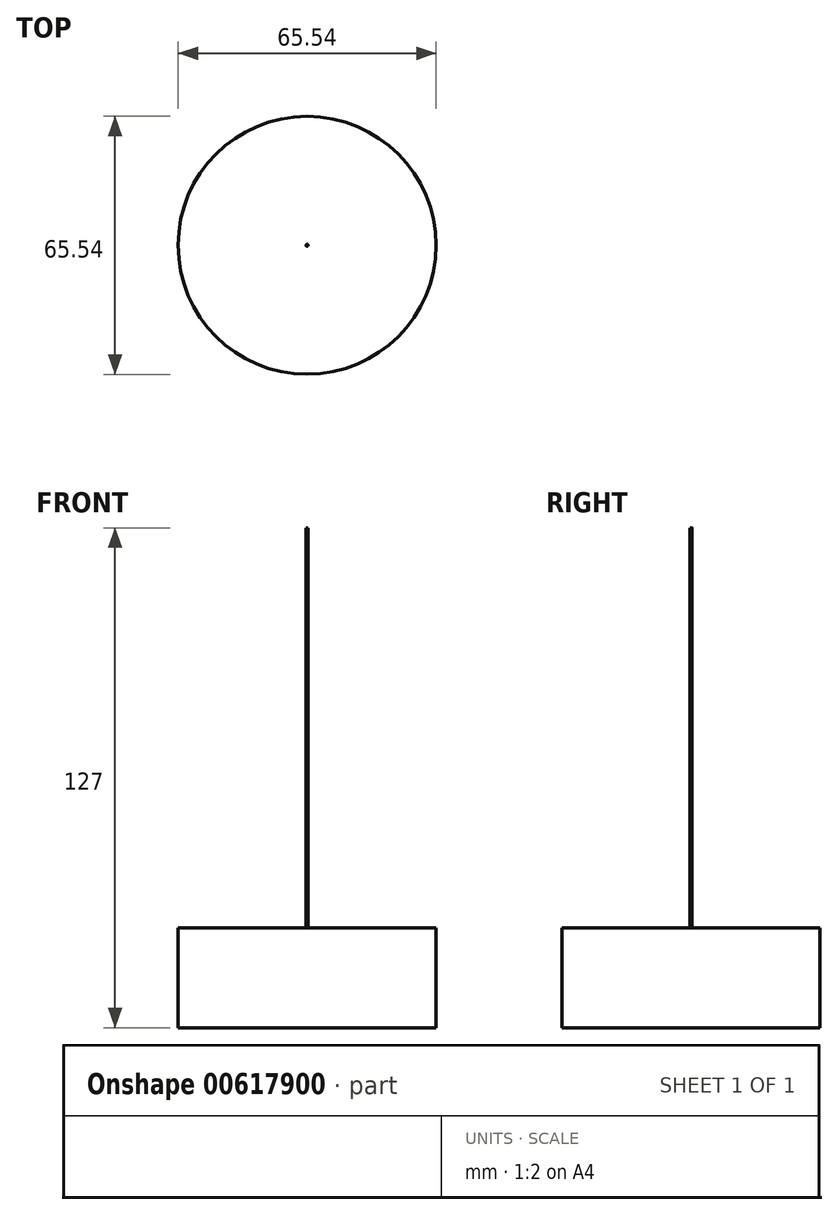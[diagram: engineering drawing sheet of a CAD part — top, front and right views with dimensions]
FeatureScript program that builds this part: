
annotation { "Feature Type Name" : "Feature", "Feature Type Description" : "" }
export const myFeature = defineFeature(function(context is Context, id is Id, definition is map)
    precondition{}
    {
        {
            var Q0;
            Q0=qCreatedBy(makeId("Front.planeOp"),FACE);
            var sketch = newSketch(context, id + "F0", { "sketchPlane" : qUnion([Q0])});
            skLineSegment(sketch, "E0.bottom", {"start": v(0, 0) * mm, "end": v(32.77, 0) * mm});
            skLineSegment(sketch, "E0.top", {"start": v(0, 25.4) * mm, "end": v(32.77, 25.4) * mm});
            skLineSegment(sketch, "E0.left", {"start": v(0, 0) * mm, "end": v(0, 25.4) * mm});
            skLineSegment(sketch, "E0.right", {"start": v(32.77, 0) * mm, "end": v(32.77, 25.4) * mm});
            skLineSegment(sketch, "E1", {"start": v(0, 0) * mm, "end": v(0, 127) * mm});
            skLineSegment(sketch, "E2", {"start": v(0, 127) * mm, "end": v(0.25, 127) * mm});
            skLineSegment(sketch, "E3", {"start": v(0.25, 127) * mm, "end": v(0.25, 0) * mm});
            skLineSegment(sketch, "E4", {"start": v(0.25, 0) * mm, "end": v(0, 0) * mm});
            skSolve(sketch);
        }
        {
            var Q0;
            Q0 = qSketchRegion(id + "F0", true);
            var Q1;
            Q1=sQuery(id+"F0.wireOp",EDGE,"E1");
            revolve(context, id + "F1", {"entities" : qUnion([Q0]), "axis" : qUnion([Q1]), "revolveType" : RevolveType.FULL});
        }
    });
